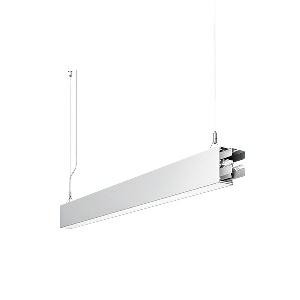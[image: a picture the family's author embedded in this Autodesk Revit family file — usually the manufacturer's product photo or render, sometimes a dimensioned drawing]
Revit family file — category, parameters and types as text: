
# Revit family: idoo_line_-_ilp_3000_830_d_sta_00805722_6681
name_source: partatom
category: Lighting Fixtures
units: mm (PartAtom-declared; Revit-internal decimal feet)

## family parameters
Cut with Voids When Loaded = No
Host = Face
Light Source = No
Part Type = Normal
Room Calculation Point = No
Round Connector Dimension = Use Diameter
Shared = No

## types (1)
- IDOO.line - ILP 3000/830/D STA (1 x LED, 3000 lm, 3000K)
    Apparent Load = 23 VA
    Approval mark = CE
    CIE Flux Codes = 66 91 98 40 100
    Color Rendering = 80-89
    Color Temperature = 3000K
    Control Gear = Electronic ballast
    Default Elevation = 1800 mm
    Description = ILP 3000/830/D|Suspended luminaire|light source: LED|connected load: 220-240 V, 50/60 Hz|Power consumption: approx. 23 W|standby: approx. 0,20|luminous flux: 3000 lm|luminous efficacy: 130 lm/W|light distribution: Direct/indirect|direct ratio: approx. 40 %|colour temperature: Warm white, ca. 3000 K|color rendering index (CRI): >= 80|chromaticity tolerance:  3 SDCM|System of protection: IP 40|technology: Continuously dimmable|luminaire body|material: Sectional aluminium|colour: White|lamp cover: Acrylic (PMMA), Clear|mains lead: 2.00 m With free stranded wires|Fastening: Steel cable 0.3 - 0.7 m|glare control: Prism aperture|luminance(L65): <= 2700 cd/m|unified glare rating(4H 8H): <=  16|special features: DALI Load 1x, TouchDIM - dimming via standard switch, Through-wired, up to 18 m on one mains connection, Flicker-free, Suitable as emergency lighting, Start luminaire with mains connection, Mechanical and electrical connection of the individual modules without tools|
    Frequency = 50 Hz
    Height = 110 mm
    Lamp = 1 x LED
    Lamp Light Flux = 3000 lm
    Lamp count = 1
    Length = 1128 mm
    Luminous efficacy = 130 lm/W
    Manufacturer = Waldmann
    ModVariant = No
    Model = 00805722
    Mounting Place = Ceiling
    Mounting Type = Pendant
    Number of Poles = 1
    OnlyDefault = Yes
    Power Factor = 1
    Product Name = IDOO.line - ILP 3000/830/D STA
    Product group = Suspended luminaire
    ProductGroupID = 9
    Protection Class = Protection class I
    Protection Degree = IP 40
    RLX_Detail_Level = 1
    RLX_Emergency_Light_Flux = 0 lm
    RLX_Emergency_Type = 0
    RLX_Emergency_Type_DB = No
    RlxData = <blob elided: 20817 chars, md5=c7f48909>
    Socket = socket
    Standby Power = 0 W
    System Light Flux = 3000 lm
    System Power = 23 W
    Type Comments = Product without accessories
    Type Image = 113301000-00692567.jpg
    URL = http://relux.com
    VarID = ---
    Voltage = 230 V
    Voltage Range = 220-240 V
    Weight = 0.00 kg
    Width = 60 mm  [stored 0.19685 ft]

note: [stored X ft] marks values corroborated as IEEE doubles in the binary element streams (Revit-internal decimal feet)

## geometry (parser evidence)
native form markers: Blend x4, Sweep x13
no freeform markers — native parametric forms only
